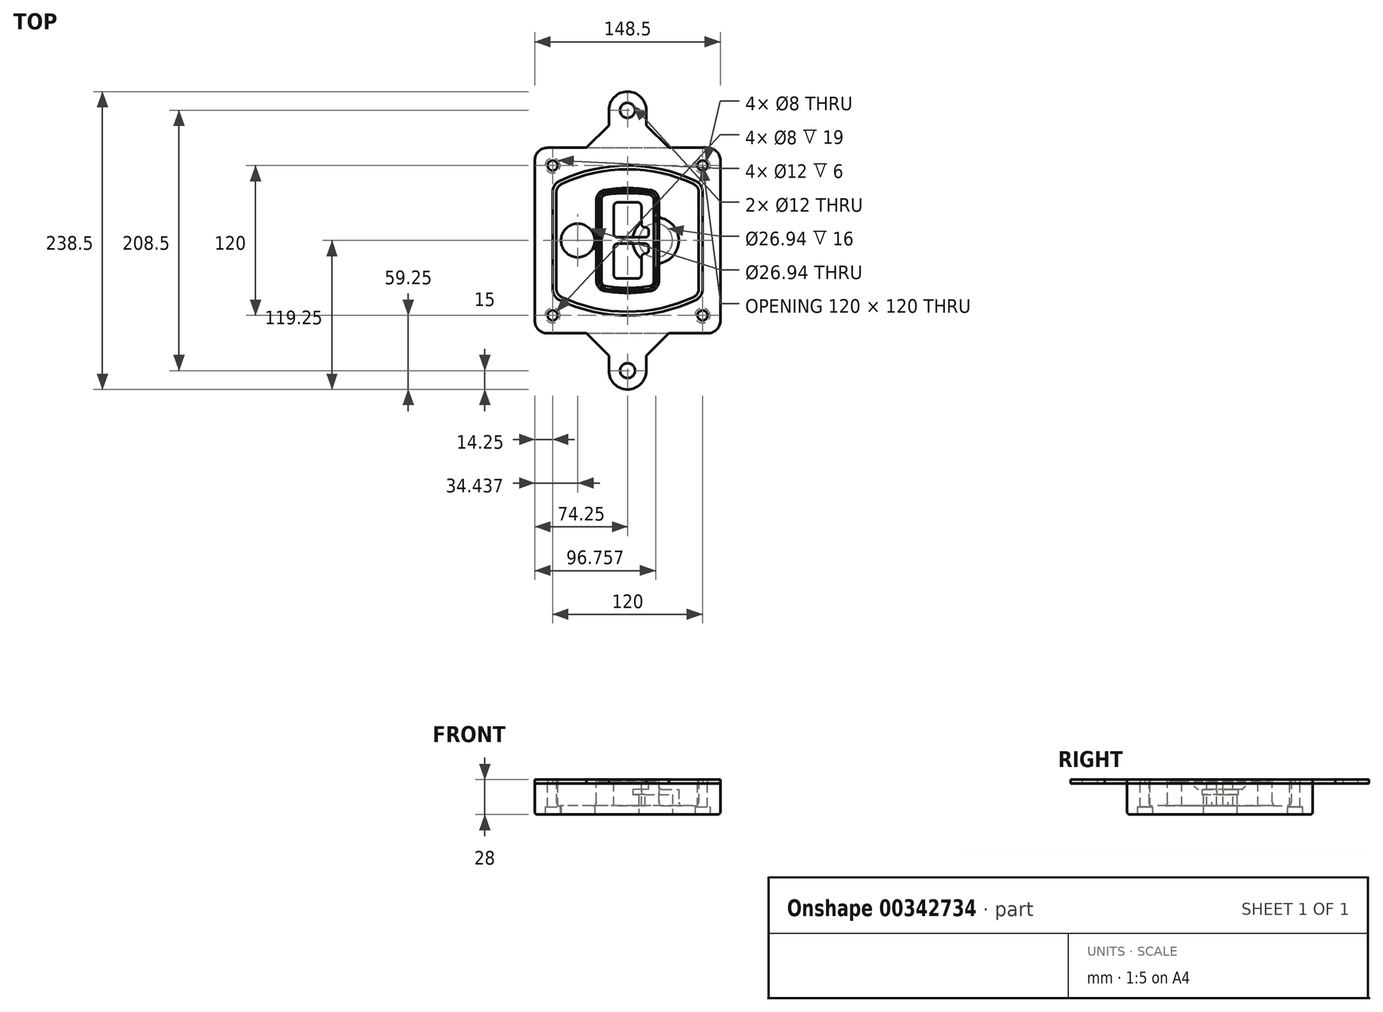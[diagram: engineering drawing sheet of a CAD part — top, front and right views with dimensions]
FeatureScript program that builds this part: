
annotation { "Feature Type Name" : "Feature", "Feature Type Description" : "" }
export const myFeature = defineFeature(function(context is Context, id is Id, definition is map)
    precondition{}
    {
        {
            var Q0;
            Q0=qCreatedBy(makeId("Top.planeOp"),FACE);
            var sketch = newSketch(context, id + "F0", { "sketchPlane" : qUnion([Q0])});
            skPoint(sketch, "E0.rect.middle", {"position": v(0, 0) * mm});
            skLineSegment(sketch, "E1.bottom", {"start": v(-64.25, -74.25) * mm, "end": v(64.25, -74.25) * mm});
            skLineSegment(sketch, "E1.top", {"start": v(-64.25, 74.25) * mm, "end": v(64.25, 74.25) * mm});
            skLineSegment(sketch, "E1.left", {"start": v(-74.25, -64.25) * mm, "end": v(-74.25, 64.25) * mm});
            skLineSegment(sketch, "E1.right", {"start": v(74.25, -64.25) * mm, "end": v(74.25, 64.25) * mm});
            skLineSegment(sketch, "E2", {"start": v(-74.25, 74.25) * mm, "end": v(74.25, -74.25) * mm, "construction": true});
            skLineSegment(sketch, "E3", {"start": v(74.25, 74.25) * mm, "end": v(-74.25, -74.25) * mm, "construction": true});
            skCircle(sketch, "E4", {"center": v(-60, 60) * mm, "radius": 4 * mm});
            skCircle(sketch, "E5", {"center": v(60, 60) * mm, "radius": 4 * mm});
            skCircle(sketch, "E6", {"center": v(60, -60) * mm, "radius": 4 * mm});
            skCircle(sketch, "E7", {"center": v(-60, -60) * mm, "radius": 4 * mm});
            skLineSegment(sketch, "E8", {"start": v(-60, 60) * mm, "end": v(60, 60) * mm, "construction": true});
            skLineSegment(sketch, "E9", {"start": v(60, 60) * mm, "end": v(60, -60) * mm, "construction": true});
            skLineSegment(sketch, "E10", {"start": v(60, -60) * mm, "end": v(-60, -60) * mm, "construction": true});
            skLineSegment(sketch, "E11", {"start": v(-60, -60) * mm, "end": v(-60, 60) * mm, "construction": true});
            skLineSegment(sketch, "E12", {"start": v(-60, 38.83) * mm, "end": v(-60, -38.83) * mm});
            skLineSegment(sketch, "E13", {"start": v(60, 38.83) * mm, "end": v(60, -38.83) * mm});
            skArc(sketch, "E14", {"start": v(54.26, 47.88) * mm, "mid": v(0, 60) * mm, "end": v(-54.26, 47.88) * mm});
            skArc(sketch, "E15", {"start": v(-54.26, -47.88) * mm, "mid": v(0, -60) * mm, "end": v(54.26, -47.88) * mm});
            skLineSegment(sketch, "E16", {"start": v(-60, 0) * mm, "end": v(60, 0) * mm, "construction": true});
            skPoint(sketch, "E17.visualSharp", {"position": v(-60, -45) * mm});
            skArc(sketch, "E17.filletArc", {"start": v(-60, -38.83) * mm, "mid": v(-58.44, -44.2) * mm, "end": v(-54.26, -47.88) * mm});
            skPoint(sketch, "E18.visualSharp", {"position": v(-60, 45) * mm});
            skArc(sketch, "E18.filletArc", {"start": v(-54.26, 47.88) * mm, "mid": v(-58.44, 44.2) * mm, "end": v(-60, 38.83) * mm});
            skPoint(sketch, "E19.visualSharp", {"position": v(60, 45) * mm});
            skArc(sketch, "E19.filletArc", {"start": v(60, 38.83) * mm, "mid": v(58.44, 44.2) * mm, "end": v(54.26, 47.88) * mm});
            skPoint(sketch, "E20.visualSharp", {"position": v(60, -45) * mm});
            skArc(sketch, "E20.filletArc", {"start": v(54.26, -47.88) * mm, "mid": v(58.44, -44.2) * mm, "end": v(60, -38.83) * mm});
            skPoint(sketch, "E21.visualSharp", {"position": v(-74.25, 74.25) * mm});
            skArc(sketch, "E21.filletArc", {"start": v(-64.25, 74.25) * mm, "mid": v(-71.32, 71.32) * mm, "end": v(-74.25, 64.25) * mm});
            skPoint(sketch, "E22.visualSharp", {"position": v(74.25, 74.25) * mm});
            skArc(sketch, "E22.filletArc", {"start": v(74.25, 64.25) * mm, "mid": v(71.32, 71.32) * mm, "end": v(64.25, 74.25) * mm});
            skPoint(sketch, "E23.visualSharp", {"position": v(74.25, -74.25) * mm});
            skArc(sketch, "E23.filletArc", {"start": v(64.25, -74.25) * mm, "mid": v(71.32, -71.32) * mm, "end": v(74.25, -64.25) * mm});
            skPoint(sketch, "E24.visualSharp", {"position": v(-74.25, -74.25) * mm});
            skArc(sketch, "E24.filletArc", {"start": v(-74.25, -64.25) * mm, "mid": v(-71.32, -71.32) * mm, "end": v(-64.25, -74.25) * mm});
            skArc(sketch, "E25.0", {"start": v(57, 38.83) * mm, "mid": v(55.9, 42.58) * mm, "end": v(52.98, 45.17) * mm});
            skLineSegment(sketch, "E25.1", {"start": v(57, 38.83) * mm, "end": v(57, -38.83) * mm});
            skArc(sketch, "E25.2", {"start": v(52.98, -45.17) * mm, "mid": v(55.9, -42.58) * mm, "end": v(57, -38.83) * mm});
            skArc(sketch, "E25.3", {"start": v(-52.98, -45.17) * mm, "mid": v(0, -57) * mm, "end": v(52.98, -45.17) * mm});
            skArc(sketch, "E25.4", {"start": v(-57, -38.83) * mm, "mid": v(-55.9, -42.58) * mm, "end": v(-52.98, -45.17) * mm});
            skArc(sketch, "E25.5", {"start": v(52.98, 45.17) * mm, "mid": v(0, 57) * mm, "end": v(-52.98, 45.17) * mm});
            skLineSegment(sketch, "E25.6", {"start": v(-57, 38.83) * mm, "end": v(-57, -38.83) * mm});
            skArc(sketch, "E25.7", {"start": v(-52.98, 45.17) * mm, "mid": v(-55.9, 42.58) * mm, "end": v(-57, 38.83) * mm});
            skArc(sketch, "E26.0", {"start": v(-55.96, 51.5) * mm, "mid": v(-61.82, 46.33) * mm, "end": v(-64, 38.83) * mm});
            skArc(sketch, "E26.1", {"start": v(55.96, 51.5) * mm, "mid": v(0, 64) * mm, "end": v(-55.96, 51.5) * mm});
            skArc(sketch, "E26.2", {"start": v(64, 38.83) * mm, "mid": v(61.82, 46.33) * mm, "end": v(55.96, 51.5) * mm});
            skLineSegment(sketch, "E26.3", {"start": v(64, 38.83) * mm, "end": v(64, -38.83) * mm});
            skArc(sketch, "E26.4", {"start": v(55.96, -51.5) * mm, "mid": v(61.82, -46.33) * mm, "end": v(64, -38.83) * mm});
            skLineSegment(sketch, "E26.5", {"start": v(-64, 38.83) * mm, "end": v(-64, -38.83) * mm});
            skArc(sketch, "E26.6", {"start": v(-55.96, -51.5) * mm, "mid": v(0, -64) * mm, "end": v(55.96, -51.5) * mm});
            skArc(sketch, "E26.7", {"start": v(-64, -38.83) * mm, "mid": v(-61.82, -46.33) * mm, "end": v(-55.96, -51.5) * mm});
            skSolve(sketch);
        }
        {
            var Q0;
            Q0=makeQuery(id+"F0.imprint","IMPRINT",FACE,{"disambiguationData":[TD([[makeQuery(id+"F0.imprint","IMPRINT",EDGE,{"derivedFrom":sQuery(id+"F0.wireOp",EDGE,"E1.bottom")}),1.0]])]});
            var Q1;
            Q1=makeQuery(id+"F0.imprint","IMPRINT",FACE,{"disambiguationData":[TD([[makeQuery(id+"F0.imprint","IMPRINT",EDGE,{"derivedFrom":sQuery(id+"F0.wireOp",EDGE,"E12")}),1.0]])]});
            var Q2;
            Q2=makeQuery(id+"F0.imprint","IMPRINT",FACE,{"disambiguationData":[TD([[makeQuery(id+"F0.imprint","IMPRINT",EDGE,{"derivedFrom":sQuery(id+"F0.wireOp",EDGE,"E25.0")}),1.0]])]});
            var Q3;
            Q3=makeQuery(id+"F0.imprint","IMPRINT",FACE,{"disambiguationData":[TD([[makeQuery(id+"F0.imprint","IMPRINT",EDGE,{"derivedFrom":sQuery(id+"F0.wireOp",EDGE,"E12")}),-1.0]])]});
            extrude(context, id + "F1", {"entities" : qUnion([Q0, Q1, Q2, Q3]), "oppositeDirection" : true, "depth" : 25 * mm});
        }
        {
            var Q0;
            Q0=makeQuery(id+"F0.imprint","IMPRINT",FACE,{"disambiguationData":[TD([[makeQuery(id+"F0.imprint","IMPRINT",EDGE,{"derivedFrom":sQuery(id+"F0.wireOp",EDGE,"E12")}),1.0]])]});
            extrude(context, id + "F2", {"entities" : qUnion([Q0]), "operationType" : NewBodyOperationType.ADD, "depth" : 3 * mm});
        }
        {
            var Q0;
            Q0=makeQuery(id+"F0.imprint","IMPRINT",FACE,{"disambiguationData":[TD([[makeQuery(id+"F0.imprint","IMPRINT",EDGE,{"derivedFrom":sQuery(id+"F0.wireOp",EDGE,"E25.0")}),1.0]])]});
            extrude(context, id + "F3", {"entities" : qUnion([Q0]), "operationType" : NewBodyOperationType.REMOVE, "oppositeDirection" : true, "depth" : 18 * mm});
        }
        {
            var Q0;
            Q0=makeQuery(id+"F2.opExtrude","CAP_FACE",FACE,{"disambiguationData":[OSD([sQuery(id+"F0.wireOp",EDGE,"E12"),sQuery(id+"F0.wireOp",EDGE,"E13"),sQuery(id+"F0.wireOp",EDGE,"E14"),sQuery(id+"F0.wireOp",EDGE,"E15"),sQuery(id+"F0.wireOp",EDGE,"E17.filletArc"),sQuery(id+"F0.wireOp",EDGE,"E18.filletArc"),sQuery(id+"F0.wireOp",EDGE,"E19.filletArc"),sQuery(id+"F0.wireOp",EDGE,"E20.filletArc"),sQuery(id+"F0.wireOp",EDGE,"E25.0"),sQuery(id+"F0.wireOp",EDGE,"E25.1"),sQuery(id+"F0.wireOp",EDGE,"E25.2"),sQuery(id+"F0.wireOp",EDGE,"E25.3"),sQuery(id+"F0.wireOp",EDGE,"E25.4"),sQuery(id+"F0.wireOp",EDGE,"E25.5"),sQuery(id+"F0.wireOp",EDGE,"E25.6"),sQuery(id+"F0.wireOp",EDGE,"E25.7")])],"isStart":false});
            var sketch = newSketch(context, id + "F4", { "sketchPlane" : qUnion([Q0])});
            skArc(sketch, "E27.0", {"start": v(-18.34, -40.45) * mm, "mid": v(0, -42) * mm, "end": v(18.34, -40.45) * mm});
            skArc(sketch, "E28.0", {"start": v(18.34, 40.45) * mm, "mid": v(0, 42) * mm, "end": v(-18.34, 40.45) * mm});
            skLineSegment(sketch, "E29", {"start": v(-25, 32.57) * mm, "end": v(-25, -32.57) * mm});
            skLineSegment(sketch, "E30", {"start": v(25, 32.57) * mm, "end": v(25, -32.57) * mm});
            skLineSegment(sketch, "E31", {"start": v(-25, 39.1) * mm, "end": v(25, 39.1) * mm, "construction": true});
            skLineSegment(sketch, "E32", {"start": v(-25, -39.1) * mm, "end": v(25, -39.1) * mm, "construction": true});
            skPoint(sketch, "E33.visualSharp", {"position": v(-25, 39.1) * mm});
            skArc(sketch, "E33.filletArc", {"start": v(-18.34, 40.45) * mm, "mid": v(-23.11, 37.73) * mm, "end": v(-25, 32.57) * mm});
            skPoint(sketch, "E34.visualSharp", {"position": v(25, 39.1) * mm});
            skArc(sketch, "E34.filletArc", {"start": v(25, 32.57) * mm, "mid": v(23.11, 37.73) * mm, "end": v(18.34, 40.45) * mm});
            skPoint(sketch, "E35.visualSharp", {"position": v(25, -39.1) * mm});
            skArc(sketch, "E35.filletArc", {"start": v(18.34, -40.45) * mm, "mid": v(23.11, -37.73) * mm, "end": v(25, -32.57) * mm});
            skPoint(sketch, "E36.visualSharp", {"position": v(-25, -39.1) * mm});
            skArc(sketch, "E36.filletArc", {"start": v(-25, -32.57) * mm, "mid": v(-23.11, -37.73) * mm, "end": v(-18.34, -40.45) * mm});
            skArc(sketch, "E37.0", {"start": v(52.98, 45.17) * mm, "mid": v(0, 57) * mm, "end": v(-52.98, 45.17) * mm});
            skArc(sketch, "E37.1", {"start": v(-52.98, 45.17) * mm, "mid": v(-55.9, 42.58) * mm, "end": v(-57, 38.83) * mm});
            skLineSegment(sketch, "E37.2", {"start": v(-57, 38.83) * mm, "end": v(-57, -38.83) * mm});
            skArc(sketch, "E37.3", {"start": v(-57, -38.83) * mm, "mid": v(-55.9, -42.58) * mm, "end": v(-52.98, -45.17) * mm});
            skArc(sketch, "E37.4", {"start": v(-52.98, -45.17) * mm, "mid": v(0, -57) * mm, "end": v(52.98, -45.17) * mm});
            skArc(sketch, "E37.5", {"start": v(52.98, -45.17) * mm, "mid": v(55.9, -42.58) * mm, "end": v(57, -38.83) * mm});
            skLineSegment(sketch, "E37.6", {"start": v(57, 38.83) * mm, "end": v(57, -38.83) * mm});
            skArc(sketch, "E37.7", {"start": v(57, 38.83) * mm, "mid": v(55.9, 42.58) * mm, "end": v(52.98, 45.17) * mm});
            skLineSegment(sketch, "E38.0", {"start": v(23, 32.57) * mm, "end": v(23, -32.57) * mm});
            skArc(sketch, "E38.1", {"start": v(18, -38.48) * mm, "mid": v(21.58, -36.44) * mm, "end": v(23, -32.57) * mm});
            skArc(sketch, "E38.2", {"start": v(-18, -38.48) * mm, "mid": v(0, -40) * mm, "end": v(18, -38.48) * mm});
            skArc(sketch, "E38.3", {"start": v(-23, -32.57) * mm, "mid": v(-21.58, -36.44) * mm, "end": v(-18, -38.48) * mm});
            skLineSegment(sketch, "E38.4", {"start": v(-23, 32.57) * mm, "end": v(-23, -32.57) * mm});
            skArc(sketch, "E38.5", {"start": v(23, 32.57) * mm, "mid": v(21.58, 36.44) * mm, "end": v(18, 38.48) * mm});
            skArc(sketch, "E38.6", {"start": v(-18, 38.48) * mm, "mid": v(-21.58, 36.44) * mm, "end": v(-23, 32.57) * mm});
            skArc(sketch, "E38.7", {"start": v(18, 38.48) * mm, "mid": v(0, 40) * mm, "end": v(-18, 38.48) * mm});
            skArc(sketch, "E39.0", {"start": v(21, 32.57) * mm, "mid": v(20.06, 35.15) * mm, "end": v(17.67, 36.5) * mm});
            skLineSegment(sketch, "E39.1", {"start": v(21, 32.57) * mm, "end": v(21, -32.57) * mm});
            skArc(sketch, "E39.2", {"start": v(17.67, -36.5) * mm, "mid": v(20.06, -35.15) * mm, "end": v(21, -32.57) * mm});
            skArc(sketch, "E39.3", {"start": v(-17.67, -36.5) * mm, "mid": v(0, -38) * mm, "end": v(17.67, -36.5) * mm});
            skArc(sketch, "E39.4", {"start": v(-21, -32.57) * mm, "mid": v(-20.06, -35.15) * mm, "end": v(-17.67, -36.5) * mm});
            skArc(sketch, "E39.5", {"start": v(17.67, 36.5) * mm, "mid": v(0, 38) * mm, "end": v(-17.67, 36.5) * mm});
            skLineSegment(sketch, "E39.6", {"start": v(-21, 32.57) * mm, "end": v(-21, -32.57) * mm});
            skArc(sketch, "E39.7", {"start": v(-17.67, 36.5) * mm, "mid": v(-20.06, 35.15) * mm, "end": v(-21, 32.57) * mm});
            skLineSegment(sketch, "E40", {"start": v(-25, 0) * mm, "end": v(25, 0) * mm, "construction": true});
            skLineSegment(sketch, "E41", {"start": v(-11, 5.5) * mm, "end": v(-11, 27.5) * mm});
            skLineSegment(sketch, "E42", {"start": v(-8, 30.5) * mm, "end": v(8, 30.5) * mm});
            skLineSegment(sketch, "E43", {"start": v(11, 27.5) * mm, "end": v(11, 13.5) * mm});
            skLineSegment(sketch, "E44", {"start": v(14, 10.5) * mm, "end": v(14, 10.5) * mm});
            skLineSegment(sketch, "E45", {"start": v(17, 7.5) * mm, "end": v(17, 5.5) * mm});
            skLineSegment(sketch, "E46", {"start": v(14, 2.5) * mm, "end": v(-8, 2.5) * mm});
            skPoint(sketch, "E47.visualSharp", {"position": v(-11, 30.5) * mm});
            skArc(sketch, "E47.filletArc", {"start": v(-8, 30.5) * mm, "mid": v(-10.12, 29.62) * mm, "end": v(-11, 27.5) * mm});
            skPoint(sketch, "E48.visualSharp", {"position": v(11, 30.5) * mm});
            skArc(sketch, "E48.filletArc", {"start": v(11, 27.5) * mm, "mid": v(10.12, 29.62) * mm, "end": v(8, 30.5) * mm});
            skPoint(sketch, "E49.visualSharp", {"position": v(11, 10.5) * mm});
            skArc(sketch, "E49.filletArc", {"start": v(11, 13.5) * mm, "mid": v(11.88, 11.38) * mm, "end": v(14, 10.5) * mm});
            skPoint(sketch, "E50.visualSharp", {"position": v(17, 10.5) * mm});
            skArc(sketch, "E50.filletArc", {"start": v(17, 7.5) * mm, "mid": v(16.12, 9.62) * mm, "end": v(14, 10.5) * mm});
            skPoint(sketch, "E51.visualSharp", {"position": v(17, 2.5) * mm});
            skArc(sketch, "E51.filletArc", {"start": v(14, 2.5) * mm, "mid": v(16.12, 3.38) * mm, "end": v(17, 5.5) * mm});
            skPoint(sketch, "E52.visualSharp", {"position": v(-11, 2.5) * mm});
            skArc(sketch, "E52.filletArc", {"start": v(-11, 5.5) * mm, "mid": v(-10.12, 3.38) * mm, "end": v(-8, 2.5) * mm});
            skLineSegment(sketch, "E53.0.MirrorCS", {"start": v(14, -2.5) * mm, "end": v(-8, -2.5) * mm});
            skArc(sketch, "E54.0.MirrorCS", {"start": v(-11, -5.5) * mm, "mid": v(-10.12, -3.38) * mm, "end": v(-8, -2.5) * mm});
            skLineSegment(sketch, "E55.0.MirrorCS", {"start": v(-11, -5.5) * mm, "end": v(-11, -27.5) * mm});
            skArc(sketch, "E56.0.MirrorCS", {"start": v(-8, -30.5) * mm, "mid": v(-10.12, -29.62) * mm, "end": v(-11, -27.5) * mm});
            skLineSegment(sketch, "E57.0.MirrorCS", {"start": v(-8, -30.5) * mm, "end": v(8, -30.5) * mm});
            skArc(sketch, "E58.0.MirrorCS", {"start": v(11, -27.5) * mm, "mid": v(10.12, -29.62) * mm, "end": v(8, -30.5) * mm});
            skLineSegment(sketch, "E59.0.MirrorCS", {"start": v(11, -27.5) * mm, "end": v(11, -13.5) * mm});
            skArc(sketch, "E60.0.MirrorCS", {"start": v(11, -13.5) * mm, "mid": v(11.88, -11.38) * mm, "end": v(14, -10.5) * mm});
            skArc(sketch, "E61.0.MirrorCS", {"start": v(17, -7.5) * mm, "mid": v(16.12, -9.62) * mm, "end": v(14, -10.5) * mm});
            skLineSegment(sketch, "E62.0.MirrorCS", {"start": v(17, -7.5) * mm, "end": v(17, -5.5) * mm});
            skArc(sketch, "E63.0.MirrorCS", {"start": v(14, -2.5) * mm, "mid": v(16.12, -3.38) * mm, "end": v(17, -5.5) * mm});
            skSolve(sketch);
        }
        {
            var Q0;
            Q0=makeQuery(id+"F4.imprint","IMPRINT",FACE,{"disambiguationData":[TD([[makeQuery(id+"F4.imprint","IMPRINT",EDGE,{"derivedFrom":sQuery(id+"F4.wireOp",EDGE,"E27.0")}),1.0]])]});
            var Q1;
            Q1=makeQuery(id+"F4.imprint","IMPRINT",FACE,{"disambiguationData":[TD([[makeQuery(id+"F4.imprint","IMPRINT",EDGE,{"derivedFrom":sQuery(id+"F4.wireOp",EDGE,"E38.0")}),-1.0]])]});
            var Q2;
            Q2=makeQuery(id+"F4.imprint","IMPRINT",FACE,{"disambiguationData":[TD([[makeQuery(id+"F4.imprint","IMPRINT",EDGE,{"derivedFrom":sQuery(id+"F4.wireOp",EDGE,"E39.0")}),1.0]])]});
            extrude(context, id + "F5", {"entities" : qUnion([Q0, Q1, Q2]), "operationType" : NewBodyOperationType.ADD, "endBound" : BoundingType.UP_TO_NEXT, "oppositeDirection" : true, "depth" : 25 * mm});
        }
        {
            var Q0;
            Q0=makeQuery(id+"F4.imprint","IMPRINT",FACE,{"disambiguationData":[TD([[makeQuery(id+"F4.imprint","IMPRINT",EDGE,{"derivedFrom":sQuery(id+"F4.wireOp",EDGE,"E38.0")}),-1.0]])]});
            extrude(context, id + "F6", {"entities" : qUnion([Q0]), "operationType" : NewBodyOperationType.REMOVE, "oppositeDirection" : true, "depth" : 2 * mm});
        }
        {
            var Q0;
            Q0=makeQuery(id+"F1.opExtrude","CAP_FACE",FACE,{"disambiguationData":[OSD([sQuery(id+"F0.wireOp",EDGE,"E1.bottom"),sQuery(id+"F0.wireOp",EDGE,"E1.top"),sQuery(id+"F0.wireOp",EDGE,"E1.left"),sQuery(id+"F0.wireOp",EDGE,"E1.right"),sQuery(id+"F0.wireOp",EDGE,"E4"),sQuery(id+"F0.wireOp",EDGE,"E5"),sQuery(id+"F0.wireOp",EDGE,"E6"),sQuery(id+"F0.wireOp",EDGE,"E7"),sQuery(id+"F0.wireOp",EDGE,"E21.filletArc"),sQuery(id+"F0.wireOp",EDGE,"E22.filletArc"),sQuery(id+"F0.wireOp",EDGE,"E23.filletArc"),sQuery(id+"F0.wireOp",EDGE,"E24.filletArc")])],"isStart":false});
            var sketch = newSketch(context, id + "F7", { "sketchPlane" : qUnion([Q0])});
            skCircle(sketch, "E64", {"center": v(22.5, 0) * mm, "radius": 13.47 * mm});
            skCircle(sketch, "E65", {"center": v(-39.81, 0) * mm, "radius": 13.47 * mm});
            skLineSegment(sketch, "E66", {"start": v(74.25, 0) * mm, "end": v(-74.25, 0) * mm});
            skCircle(sketch, "E67", {"center": v(22.5, 0) * mm, "radius": 18.47 * mm});
            skCircle(sketch, "E68", {"center": v(60, -60) * mm, "radius": 6 * mm});
            skCircle(sketch, "E69", {"center": v(-60, -60) * mm, "radius": 6 * mm});
            skCircle(sketch, "E70", {"center": v(-60, 60) * mm, "radius": 6 * mm});
            skCircle(sketch, "E71", {"center": v(60, 60) * mm, "radius": 6 * mm});
            skSolve(sketch);
        }
        {
            var Q0;
            {var subQ1=sQuery(id+"F7.wireOp",EDGE,"E66");var subQ4=sQuery(id+"F7.wireOp",EDGE,"E64");var subQ6=makeQuery(id+"F7.imprint","INTERSECT",VERTEX,{"disambiguationData":[OD(0.0)],"derivedFrom":[subQ4,subQ1]});Q0=makeQuery(id+"F7.imprint","IMPRINT",FACE,{"disambiguationData":[TD([[makeQuery(id+"F7.imprint","IMPRINT",EDGE,{"disambiguationData":[TD([[subQ6,-1.0]])],"derivedFrom":subQ4}),-1.0]])]});}
            var Q1;
            {var subQ0=sQuery(id+"F7.wireOp",EDGE,"E66");var subQ1=sQuery(id+"F7.wireOp",EDGE,"E64");var subQ3=makeQuery(id+"F7.imprint","INTERSECT",VERTEX,{"disambiguationData":[OD(0.0)],"derivedFrom":[subQ1,subQ0]});Q1=makeQuery(id+"F7.imprint","IMPRINT",FACE,{"disambiguationData":[TD([[makeQuery(id+"F7.imprint","IMPRINT",EDGE,{"disambiguationData":[TD([[subQ3,-1.0]])],"derivedFrom":subQ1}),1.0]])]});}
            var Q2;
            {var subQ0=sQuery(id+"F7.wireOp",EDGE,"E66");var subQ1=sQuery(id+"F7.wireOp",EDGE,"E64");var subQ3=makeQuery(id+"F7.imprint","INTERSECT",VERTEX,{"disambiguationData":[OD(0.0)],"derivedFrom":[subQ1,subQ0]});Q2=makeQuery(id+"F7.imprint","IMPRINT",FACE,{"disambiguationData":[TD([[makeQuery(id+"F7.imprint","IMPRINT",EDGE,{"disambiguationData":[TD([[subQ3,1.0]])],"derivedFrom":subQ1}),1.0]])]});}
            var Q3;
            {var subQ1=sQuery(id+"F7.wireOp",EDGE,"E66");var subQ4=sQuery(id+"F7.wireOp",EDGE,"E64");var subQ6=makeQuery(id+"F7.imprint","INTERSECT",VERTEX,{"disambiguationData":[OD(0.0)],"derivedFrom":[subQ4,subQ1]});Q3=makeQuery(id+"F7.imprint","IMPRINT",FACE,{"disambiguationData":[TD([[makeQuery(id+"F7.imprint","IMPRINT",EDGE,{"disambiguationData":[TD([[subQ6,1.0]])],"derivedFrom":subQ4}),-1.0]])]});}
            extrude(context, id + "F8", {"entities" : qUnion([Q0, Q1, Q2, Q3]), "operationType" : NewBodyOperationType.ADD, "oppositeDirection" : true, "depth" : 20 * mm});
        }
        {
            var Q0;
            {var subQ0=sQuery(id+"F7.wireOp",EDGE,"E66");var subQ1=sQuery(id+"F7.wireOp",EDGE,"E64");var subQ3=makeQuery(id+"F7.imprint","INTERSECT",VERTEX,{"disambiguationData":[OD(0.0)],"derivedFrom":[subQ1,subQ0]});Q0=makeQuery(id+"F7.imprint","IMPRINT",FACE,{"disambiguationData":[TD([[makeQuery(id+"F7.imprint","IMPRINT",EDGE,{"disambiguationData":[TD([[subQ3,-1.0]])],"derivedFrom":subQ1}),1.0]])]});}
            var Q1;
            {var subQ0=sQuery(id+"F7.wireOp",EDGE,"E66");var subQ1=sQuery(id+"F7.wireOp",EDGE,"E64");var subQ3=makeQuery(id+"F7.imprint","INTERSECT",VERTEX,{"disambiguationData":[OD(0.0)],"derivedFrom":[subQ1,subQ0]});Q1=makeQuery(id+"F7.imprint","IMPRINT",FACE,{"disambiguationData":[TD([[makeQuery(id+"F7.imprint","IMPRINT",EDGE,{"disambiguationData":[TD([[subQ3,1.0]])],"derivedFrom":subQ1}),1.0]])]});}
            extrude(context, id + "F9", {"entities" : qUnion([Q0, Q1]), "operationType" : NewBodyOperationType.REMOVE, "oppositeDirection" : true, "depth" : 16 * mm});
        }
        {
            var Q0;
            {var subQ0=sQuery(id+"F7.wireOp",EDGE,"E66");var subQ1=sQuery(id+"F7.wireOp",EDGE,"E65");var subQ3=makeQuery(id+"F7.imprint","INTERSECT",VERTEX,{"disambiguationData":[OD(0.0)],"derivedFrom":[subQ1,subQ0]});Q0=makeQuery(id+"F7.imprint","IMPRINT",FACE,{"disambiguationData":[TD([[makeQuery(id+"F7.imprint","IMPRINT",EDGE,{"disambiguationData":[TD([[subQ3,-1.0]])],"derivedFrom":subQ1}),1.0]])]});}
            var Q1;
            {var subQ0=sQuery(id+"F7.wireOp",EDGE,"E66");var subQ1=sQuery(id+"F7.wireOp",EDGE,"E65");var subQ3=makeQuery(id+"F7.imprint","INTERSECT",VERTEX,{"disambiguationData":[OD(0.0)],"derivedFrom":[subQ1,subQ0]});Q1=makeQuery(id+"F7.imprint","IMPRINT",FACE,{"disambiguationData":[TD([[makeQuery(id+"F7.imprint","IMPRINT",EDGE,{"disambiguationData":[TD([[subQ3,1.0]])],"derivedFrom":subQ1}),1.0]])]});}
            extrude(context, id + "F10", {"entities" : qUnion([Q0, Q1]), "operationType" : NewBodyOperationType.REMOVE, "oppositeDirection" : true, "depth" : 25 * mm});
        }
        {
            var Q0;
            Q0=makeQuery(id+"F7.imprint","IMPRINT",FACE,{"disambiguationData":[TD([[makeQuery(id+"F7.imprint","IMPRINT",EDGE,{"derivedFrom":sQuery(id+"F7.wireOp",EDGE,"E68")}),1.0]])]});
            var Q1;
            Q1=makeQuery(id+"F7.imprint","IMPRINT",FACE,{"disambiguationData":[TD([[makeQuery(id+"F7.imprint","IMPRINT",EDGE,{"derivedFrom":makeQuery(id+"F1.opExtrude","CAP_EDGE",EDGE,{"disambiguationData":[OSD([sQuery(id+"F0.wireOp",EDGE,"E5")])],"isStart":false})}),-1.0]])]});
            var Q2;
            Q2=makeQuery(id+"F7.imprint","IMPRINT",FACE,{"disambiguationData":[TD([[makeQuery(id+"F7.imprint","IMPRINT",EDGE,{"derivedFrom":sQuery(id+"F7.wireOp",EDGE,"E69")}),1.0]])]});
            var Q3;
            Q3=makeQuery(id+"F7.imprint","IMPRINT",FACE,{"disambiguationData":[TD([[makeQuery(id+"F7.imprint","IMPRINT",EDGE,{"derivedFrom":makeQuery(id+"F1.opExtrude","CAP_EDGE",EDGE,{"disambiguationData":[OSD([sQuery(id+"F0.wireOp",EDGE,"E4")])],"isStart":false})}),-1.0]])]});
            var Q4;
            Q4=makeQuery(id+"F7.imprint","IMPRINT",FACE,{"disambiguationData":[TD([[makeQuery(id+"F7.imprint","IMPRINT",EDGE,{"derivedFrom":sQuery(id+"F7.wireOp",EDGE,"E70")}),1.0]])]});
            var Q5;
            Q5=makeQuery(id+"F7.imprint","IMPRINT",FACE,{"disambiguationData":[TD([[makeQuery(id+"F7.imprint","IMPRINT",EDGE,{"derivedFrom":makeQuery(id+"F1.opExtrude","CAP_EDGE",EDGE,{"disambiguationData":[OSD([sQuery(id+"F0.wireOp",EDGE,"E7")])],"isStart":false})}),-1.0]])]});
            var Q6;
            Q6=makeQuery(id+"F7.imprint","IMPRINT",FACE,{"disambiguationData":[TD([[makeQuery(id+"F7.imprint","IMPRINT",EDGE,{"derivedFrom":sQuery(id+"F7.wireOp",EDGE,"E71")}),1.0]])]});
            var Q7;
            Q7=makeQuery(id+"F7.imprint","IMPRINT",FACE,{"disambiguationData":[TD([[makeQuery(id+"F7.imprint","IMPRINT",EDGE,{"derivedFrom":makeQuery(id+"F1.opExtrude","CAP_EDGE",EDGE,{"disambiguationData":[OSD([sQuery(id+"F0.wireOp",EDGE,"E6")])],"isStart":false})}),-1.0]])]});
            extrude(context, id + "F11", {"entities" : qUnion([Q0, Q1, Q2, Q3, Q4, Q5, Q6, Q7]), "operationType" : NewBodyOperationType.REMOVE, "oppositeDirection" : true, "depth" : 6 * mm});
        }
        {
            var Q0;
            Q0=makeQuery(id+"F9.boolean.opBoolean","COPY",FACE,{"derivedFrom":makeQuery(id+"F9.opExtrude","CAP_FACE",FACE,{"disambiguationData":[OSD([sQuery(id+"F7.wireOp",EDGE,"E64")])],"isStart":false})});
            var sketch = newSketch(context, id + "F12", { "sketchPlane" : qUnion([Q0])});
            skArc(sketch, "E72.0", {"start": v(11, 14.45) * mm, "mid": v(6.45, 9.13) * mm, "end": v(4.2, 2.5) * mm});
            skArc(sketch, "E72.1", {"start": v(4.2, -2.5) * mm, "mid": v(6.45, -9.13) * mm, "end": v(11, -14.45) * mm});
            skLineSegment(sketch, "E73", {"start": v(4.2, -2.5) * mm, "end": v(14, -2.5) * mm});
            skLineSegment(sketch, "E74.0", {"start": v(14, 2.5) * mm, "end": v(4.2, 2.5) * mm});
            skArc(sketch, "E74.1", {"start": v(14, 2.5) * mm, "mid": v(16.12, 3.38) * mm, "end": v(17, 5.5) * mm});
            skLineSegment(sketch, "E74.2", {"start": v(17, 7.5) * mm, "end": v(17, 5.5) * mm});
            skArc(sketch, "E74.3", {"start": v(17, 7.5) * mm, "mid": v(16.12, 9.62) * mm, "end": v(14, 10.5) * mm});
            skArc(sketch, "E74.4", {"start": v(11, 13.5) * mm, "mid": v(11.88, 11.38) * mm, "end": v(14, 10.5) * mm});
            skLineSegment(sketch, "E74.5", {"start": v(11, 14.45) * mm, "end": v(11, 13.5) * mm});
            skLineSegment(sketch, "E74.7", {"start": v(14, -2.5) * mm, "end": v(4.2, -2.5) * mm});
            skArc(sketch, "E74.8", {"start": v(14, -2.5) * mm, "mid": v(16.12, -3.38) * mm, "end": v(17, -5.5) * mm});
            skLineSegment(sketch, "E74.9", {"start": v(17, -7.5) * mm, "end": v(17, -5.5) * mm});
            skArc(sketch, "E74.10", {"start": v(17, -7.5) * mm, "mid": v(16.12, -9.62) * mm, "end": v(14, -10.5) * mm});
            skArc(sketch, "E74.11", {"start": v(11, -13.5) * mm, "mid": v(11.88, -11.38) * mm, "end": v(14, -10.5) * mm});
            skLineSegment(sketch, "E74.12", {"start": v(11, -14.45) * mm, "end": v(11, -13.5) * mm});
            skPoint(sketch, "E75.orphan", {"position": v(11, -27.5) * mm});
            skPoint(sketch, "E76.orphan", {"position": v(-8, -2.5) * mm});
            skPoint(sketch, "E77.orphan", {"position": v(-8, 2.5) * mm});
            skPoint(sketch, "E78.orphan", {"position": v(11, 27.5) * mm});
            skSolve(sketch);
        }
        {
            var Q0;
            {var subQ7=sQuery(id+"F12.wireOp",EDGE,"E72.0");var subQ14=sQuery(id+"F12.wireOp",EDGE,"E72.1");var subQ16=sQuery(id+"F12.wireOp",EDGE,"E74.1");var subQ18=sQuery(id+"F12.wireOp",EDGE,"E74.8");Q0=qUnion([makeQuery(id+"F12.imprint","IMPRINT",FACE,{"disambiguationData":[TD([[makeQuery(id+"F12.imprint","IMPRINT",EDGE,{"derivedFrom":subQ7}),1.0]])]}),makeQuery(id+"F12.imprint","IMPRINT",FACE,{"disambiguationData":[TD([[makeQuery(id+"F12.imprint","IMPRINT",EDGE,{"derivedFrom":subQ14}),1.0]])]}),makeQuery(id+"F12.imprint","IMPRINT",FACE,{"disambiguationData":[TD([[makeQuery(id+"F12.imprint","IMPRINT",EDGE,{"derivedFrom":subQ16}),1.0]])]}),makeQuery(id+"F12.imprint","IMPRINT",FACE,{"disambiguationData":[TD([[makeQuery(id+"F12.imprint","IMPRINT",EDGE,{"derivedFrom":subQ18}),-1.0]])]})]);}
            var Q1;
            Q1=makeQuery(id+"F5.boolean.opBoolean","SPLIT",FACE,{"disambiguationData":[TD([makeQuery(id+"F5.opExtrude","SWEPT_FACE",FACE,{"disambiguationData":[OSD([sQuery(id+"F4.wireOp",EDGE,"E41")])]})])],"derivedFrom":makeQuery(id+"F3.boolean.opBoolean","COPY",FACE,{"derivedFrom":makeQuery(id+"F3.opExtrude","CAP_FACE",FACE,{"disambiguationData":[OSD([sQuery(id+"F0.wireOp",EDGE,"E25.0"),sQuery(id+"F0.wireOp",EDGE,"E25.1"),sQuery(id+"F0.wireOp",EDGE,"E25.2"),sQuery(id+"F0.wireOp",EDGE,"E25.3"),sQuery(id+"F0.wireOp",EDGE,"E25.4"),sQuery(id+"F0.wireOp",EDGE,"E25.5"),sQuery(id+"F0.wireOp",EDGE,"E25.6"),sQuery(id+"F0.wireOp",EDGE,"E25.7")])],"isStart":false})})});
            extrude(context, id + "F13", {"entities" : qUnion([Q0]), "operationType" : NewBodyOperationType.REMOVE, "endBound" : BoundingType.UP_TO_SURFACE, "endBoundEntityFace" : qUnion([Q1]), "depth" : 25 * mm});
        }
        {
            var Q0;
            Q0=makeQuery(id+"F3.boolean.opBoolean","COPY",EDGE,{"derivedFrom":makeQuery(id+"F3.opExtrude","CAP_EDGE",EDGE,{"disambiguationData":[OSD([sQuery(id+"F0.wireOp",EDGE,"E25.6")])],"isStart":false})});
            var Q1;
            Q1=makeQuery(id+"F8.boolean.opBoolean","INTERSECT",EDGE,{"derivedFrom":[makeQuery(id+"F5.opExtrude","SWEPT_FACE",FACE,{"disambiguationData":[OSD([sQuery(id+"F4.wireOp",EDGE,"E30")])]}),makeQuery(id+"F8.opExtrude","CAP_FACE",FACE,{"disambiguationData":[OSD([sQuery(id+"F7.wireOp",EDGE,"E67")])],"isStart":false})]});
            var Q2;
            Q2=makeQuery(id+"F8.boolean.opBoolean","INTERSECT",EDGE,{"disambiguationData":[OD(1.0)],"derivedFrom":[makeQuery(id+"F5.opExtrude","SWEPT_FACE",FACE,{"disambiguationData":[OSD([sQuery(id+"F4.wireOp",EDGE,"E30")])]}),makeQuery(id+"F8.opExtrude","SWEPT_FACE",FACE,{"disambiguationData":[OSD([sQuery(id+"F7.wireOp",EDGE,"E67")])]})]});
            var Q3;
            {var subQ0=sQuery(id+"F4.wireOp",EDGE,"E30");Q3=makeQuery(id+"F8.boolean.opBoolean","SPLIT",EDGE,{"disambiguationData":[TD([makeQuery(id+"F5.opExtrude","SWEPT_FACE",FACE,{"disambiguationData":[OSD([sQuery(id+"F4.wireOp",EDGE,"E35.filletArc")])]})])],"derivedFrom":makeQuery(id+"F5.opExtrude","CAP_EDGE",EDGE,{"disambiguationData":[OSD([subQ0])],"isStart":false})});}
            var Q4;
            {var subQ0=sQuery(id+"F0.wireOp",EDGE,"E25.7");var subQ1=sQuery(id+"F0.wireOp",EDGE,"E25.1");var subQ2=sQuery(id+"F0.wireOp",EDGE,"E25.6");var subQ3=sQuery(id+"F0.wireOp",EDGE,"E25.5");var subQ4=sQuery(id+"F0.wireOp",EDGE,"E25.4");var subQ5=sQuery(id+"F0.wireOp",EDGE,"E25.0");var subQ6=sQuery(id+"F0.wireOp",EDGE,"E25.2");var subQ7=sQuery(id+"F0.wireOp",EDGE,"E25.3");Q4=makeQuery(id+"F8.boolean.opBoolean","INTERSECT",EDGE,{"derivedFrom":[makeQuery(id+"F5.boolean.opBoolean","SPLIT",FACE,{"disambiguationData":[TD([makeQuery(id+"F2.opExtrude","SWEPT_FACE",FACE,{"disambiguationData":[OSD([subQ5])]})])],"derivedFrom":makeQuery(id+"F3.boolean.opBoolean","COPY",FACE,{"derivedFrom":makeQuery(id+"F3.opExtrude","CAP_FACE",FACE,{"disambiguationData":[OSD([subQ5,subQ1,subQ6,subQ7,subQ4,subQ3,subQ2,subQ0])],"isStart":false})})}),makeQuery(id+"F8.opExtrude","SWEPT_FACE",FACE,{"disambiguationData":[OSD([sQuery(id+"F7.wireOp",EDGE,"E67")])]})]});}
            var Q5;
            Q5=makeQuery(id+"F8.boolean.opBoolean","INTERSECT",EDGE,{"disambiguationData":[OD(0.0)],"derivedFrom":[makeQuery(id+"F5.opExtrude","SWEPT_FACE",FACE,{"disambiguationData":[OSD([sQuery(id+"F4.wireOp",EDGE,"E30")])]}),makeQuery(id+"F8.opExtrude","SWEPT_FACE",FACE,{"disambiguationData":[OSD([sQuery(id+"F7.wireOp",EDGE,"E67")])]})]});
            fillet(context, id + "F14", {"entities" : qUnion([Q0, Q1, Q2, Q3, Q4, Q5]), "radius" : 3 * mm, "tangentPropagation" : true, "allowEdgeOverflow" : false});
        }
        {
            var Q0;
            Q0=makeQuery(id+"F1.opExtrude","CAP_EDGE",EDGE,{"disambiguationData":[OSD([sQuery(id+"F0.wireOp",EDGE,"E1.bottom")])],"isStart":false});
            fillet(context, id + "F15", {"entities" : qUnion([Q0]), "radius" : 2 * mm, "tangentPropagation" : true, "allowEdgeOverflow" : false});
        }
        {
            var Q0;
            {var subQ0=sQuery(id+"F0.wireOp",EDGE,"E21.filletArc");var subQ1=sQuery(id+"F0.wireOp",EDGE,"E7");var subQ2=sQuery(id+"F0.wireOp",EDGE,"E6");var subQ3=sQuery(id+"F0.wireOp",EDGE,"E5");var subQ4=sQuery(id+"F0.wireOp",EDGE,"E4");var subQ5=sQuery(id+"F0.wireOp",EDGE,"E22.filletArc");var subQ6=sQuery(id+"F0.wireOp",EDGE,"E1.bottom");var subQ7=sQuery(id+"F0.wireOp",EDGE,"E1.right");var subQ8=sQuery(id+"F0.wireOp",EDGE,"E1.top");var subQ9=sQuery(id+"F0.wireOp",EDGE,"E1.left");var subQ10=sQuery(id+"F0.wireOp",EDGE,"E23.filletArc");var subQ11=sQuery(id+"F0.wireOp",EDGE,"E24.filletArc");Q0=makeQuery(id+"F2.boolean.opBoolean","SPLIT",FACE,{"disambiguationData":[TD([makeQuery(id+"F1.opExtrude","SWEPT_FACE",FACE,{"disambiguationData":[OSD([subQ6])]})])],"derivedFrom":makeQuery(id+"F1.opExtrude","CAP_FACE",FACE,{"disambiguationData":[OSD([subQ6,subQ8,subQ9,subQ7,subQ4,subQ3,subQ2,subQ1,subQ0,subQ5,subQ10,subQ11])],"isStart":true})});}
            var sketch = newSketch(context, id + "F16", { "sketchPlane" : qUnion([Q0])});
            skLineSegment(sketch, "E79.0", {"start": v(-64.25, 74.25) * mm, "end": v(64.25, 74.25) * mm});
            skArc(sketch, "E79.1", {"start": v(-64.25, 74.25) * mm, "mid": v(-71.32, 71.32) * mm, "end": v(-74.25, 64.25) * mm});
            skLineSegment(sketch, "E79.2", {"start": v(-74.25, -64.25) * mm, "end": v(-74.25, 64.25) * mm});
            skArc(sketch, "E79.3", {"start": v(-74.25, -64.25) * mm, "mid": v(-71.32, -71.32) * mm, "end": v(-64.25, -74.25) * mm});
            skLineSegment(sketch, "E79.4", {"start": v(-64.25, -74.25) * mm, "end": v(64.25, -74.25) * mm});
            skArc(sketch, "E79.5", {"start": v(64.25, -74.25) * mm, "mid": v(71.32, -71.32) * mm, "end": v(74.25, -64.25) * mm});
            skLineSegment(sketch, "E79.6", {"start": v(74.25, -64.25) * mm, "end": v(74.25, 64.25) * mm});
            skArc(sketch, "E79.7", {"start": v(74.25, 64.25) * mm, "mid": v(71.32, 71.32) * mm, "end": v(64.25, 74.25) * mm});
            skCircle(sketch, "E79.8", {"center": v(60, 60) * mm, "radius": 4 * mm});
            skCircle(sketch, "E79.9", {"center": v(-60, -60) * mm, "radius": 4 * mm});
            skCircle(sketch, "E79.10", {"center": v(60, -60) * mm, "radius": 4 * mm});
            skArc(sketch, "E79.11", {"start": v(54.26, 47.88) * mm, "mid": v(0, 60) * mm, "end": v(-54.26, 47.88) * mm});
            skArc(sketch, "E79.12", {"start": v(-54.26, 47.88) * mm, "mid": v(-58.44, 44.2) * mm, "end": v(-60, 38.83) * mm});
            skLineSegment(sketch, "E79.13", {"start": v(-60, 38.83) * mm, "end": v(-60, -38.83) * mm});
            skArc(sketch, "E79.14", {"start": v(-60, -38.83) * mm, "mid": v(-58.44, -44.2) * mm, "end": v(-54.26, -47.88) * mm});
            skArc(sketch, "E79.15", {"start": v(-54.26, -47.88) * mm, "mid": v(0, -60) * mm, "end": v(54.26, -47.88) * mm});
            skLineSegment(sketch, "E79.16", {"start": v(60, 38.83) * mm, "end": v(60, -38.83) * mm});
            skArc(sketch, "E79.17", {"start": v(54.26, -47.88) * mm, "mid": v(58.44, -44.2) * mm, "end": v(60, -38.83) * mm});
            skArc(sketch, "E79.18", {"start": v(60, 38.83) * mm, "mid": v(58.44, 44.2) * mm, "end": v(54.26, 47.88) * mm});
            skCircle(sketch, "E79.19", {"center": v(-60, 60) * mm, "radius": 4 * mm});
            skLineSegment(sketch, "E80", {"start": v(-33, 74.25) * mm, "end": v(-15, 92.25) * mm});
            skLineSegment(sketch, "E81", {"start": v(-15, 92.25) * mm, "end": v(-15, 104.25) * mm});
            skArc(sketch, "E82", {"start": v(15, 104.25) * mm, "mid": v(0, 119.25) * mm, "end": v(-15, 104.25) * mm});
            skLineSegment(sketch, "E83", {"start": v(15, 104.25) * mm, "end": v(15, 92.25) * mm});
            skLineSegment(sketch, "E84", {"start": v(15, 92.25) * mm, "end": v(33, 74.25) * mm});
            skCircle(sketch, "E85", {"center": v(0, 104.25) * mm, "radius": 6 * mm});
            skLineSegment(sketch, "E86", {"start": v(0, 104.25) * mm, "end": v(0, 74.25) * mm, "construction": true});
            skLineSegment(sketch, "E87", {"start": v(-74.25, 0) * mm, "end": v(74.25, 0) * mm, "construction": true});
            skLineSegment(sketch, "E88.MirrorCS", {"start": v(-33, -74.25) * mm, "end": v(-15, -92.25) * mm});
            skLineSegment(sketch, "E89.MirrorCS", {"start": v(-15, -92.25) * mm, "end": v(-15, -104.25) * mm});
            skArc(sketch, "E90.MirrorCS", {"start": v(15, -104.25) * mm, "mid": v(0, -119.25) * mm, "end": v(-15, -104.25) * mm});
            skLineSegment(sketch, "E91.MirrorCS", {"start": v(15, -104.25) * mm, "end": v(15, -92.25) * mm});
            skLineSegment(sketch, "E92.MirrorCS", {"start": v(15, -92.25) * mm, "end": v(33, -74.25) * mm});
            skCircle(sketch, "E93.MirrorC", {"center": v(0, -104.25) * mm, "radius": 6 * mm});
            skLineSegment(sketch, "E94.MirrorCS", {"start": v(0, -104.25) * mm, "end": v(0, -74.25) * mm, "construction": true});
            skSolve(sketch);
        }
        {
            var Q0;
            {var subQ0=sQuery(id+"F16.wireOp",EDGE,"E80");Q0=makeQuery(id+"F16.imprint","IMPRINT",FACE,{"disambiguationData":[TD([[makeQuery(id+"F16.imprint","IMPRINT",EDGE,{"derivedFrom":subQ0}),-1.0]])]});}
            var Q1;
            {var subQ1=sQuery(id+"F16.wireOp",EDGE,"E79.1");Q1=makeQuery(id+"F16.imprint","IMPRINT",FACE,{"disambiguationData":[TD([[makeQuery(id+"F16.imprint","IMPRINT",EDGE,{"derivedFrom":subQ1}),1.0]])]});}
            var Q2;
            {var subQ0=sQuery(id+"F16.wireOp",EDGE,"E88.MirrorCS");Q2=makeQuery(id+"F16.imprint","IMPRINT",FACE,{"disambiguationData":[TD([[makeQuery(id+"F16.imprint","IMPRINT",EDGE,{"derivedFrom":subQ0}),1.0]])]});}
            var Q3;
            Q3=makeQuery(id+"F2.opExtrude","CAP_FACE",FACE,{"disambiguationData":[OSD([sQuery(id+"F0.wireOp",EDGE,"E12"),sQuery(id+"F0.wireOp",EDGE,"E13"),sQuery(id+"F0.wireOp",EDGE,"E14"),sQuery(id+"F0.wireOp",EDGE,"E15"),sQuery(id+"F0.wireOp",EDGE,"E17.filletArc"),sQuery(id+"F0.wireOp",EDGE,"E18.filletArc"),sQuery(id+"F0.wireOp",EDGE,"E19.filletArc"),sQuery(id+"F0.wireOp",EDGE,"E20.filletArc"),sQuery(id+"F0.wireOp",EDGE,"E25.0"),sQuery(id+"F0.wireOp",EDGE,"E25.1"),sQuery(id+"F0.wireOp",EDGE,"E25.2"),sQuery(id+"F0.wireOp",EDGE,"E25.3"),sQuery(id+"F0.wireOp",EDGE,"E25.4"),sQuery(id+"F0.wireOp",EDGE,"E25.5"),sQuery(id+"F0.wireOp",EDGE,"E25.6"),sQuery(id+"F0.wireOp",EDGE,"E25.7")])],"isStart":false});
            extrude(context, id + "F17", {"entities" : qUnion([Q0, Q1, Q2]), "endBound" : BoundingType.UP_TO_SURFACE, "endBoundEntityFace" : qUnion([Q3]), "depth" : 25 * mm});
        }
    });
